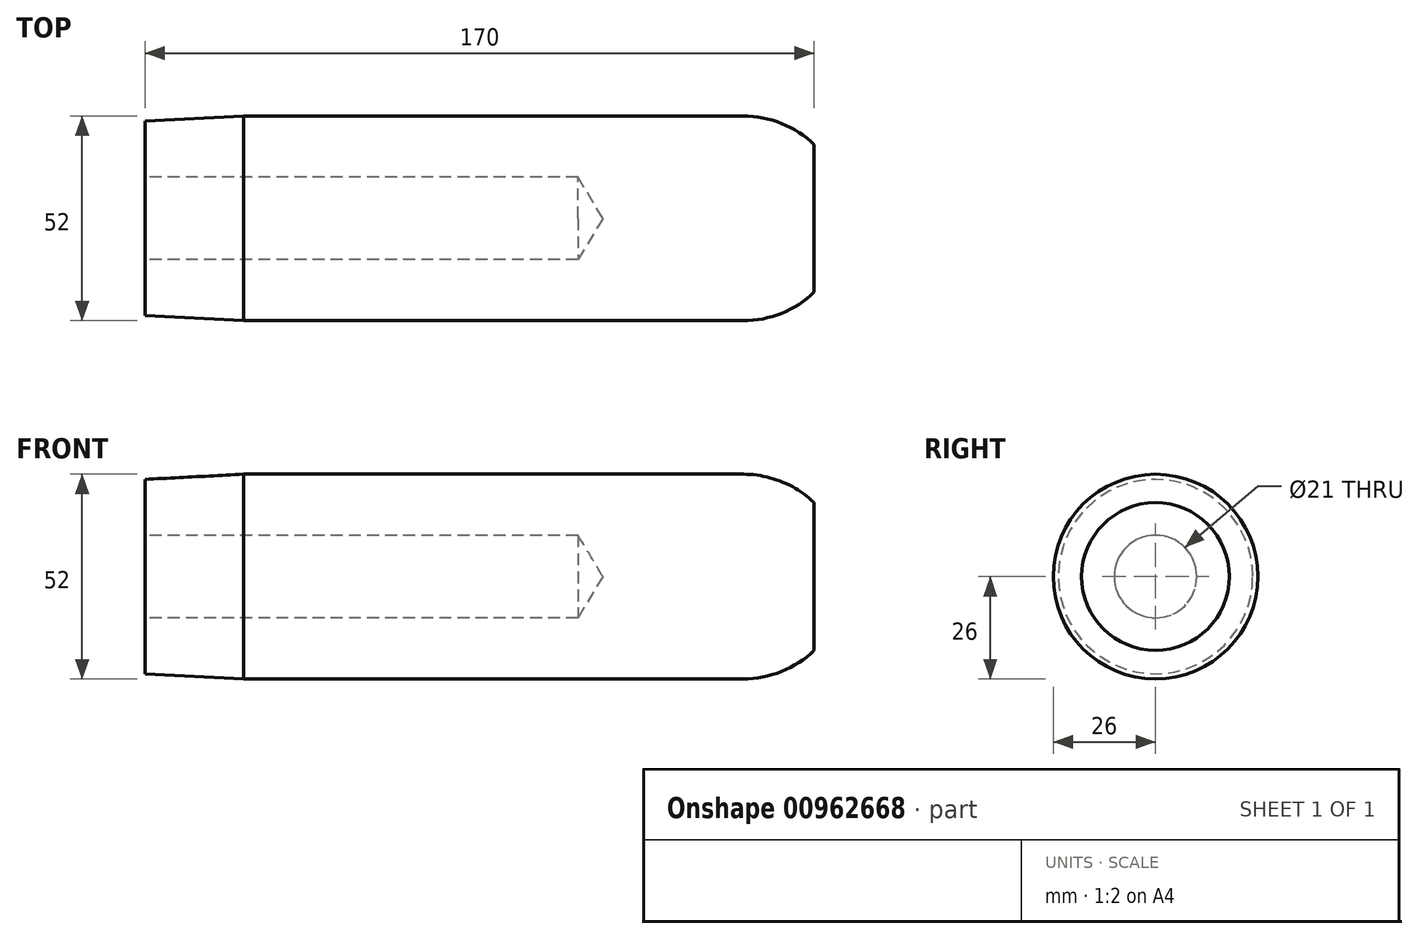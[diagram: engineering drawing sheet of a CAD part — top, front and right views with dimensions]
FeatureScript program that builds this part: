
annotation { "Feature Type Name" : "Feature", "Feature Type Description" : "" }
export const myFeature = defineFeature(function(context is Context, id is Id, definition is map)
    precondition{}
    {
        {
            var Q0;
            Q0=qCreatedBy(makeId("Front.planeOp"),FACE);
            var sketch = newSketch(context, id + "F0", { "sketchPlane" : qUnion([Q0])});
            skLineSegment(sketch, "E0", {"start": v(0, 0) * mm, "end": v(170, 0) * mm});
            skLineSegment(sketch, "E1", {"start": v(0, 0) * mm, "end": v(0, -24.69) * mm});
            skLineSegment(sketch, "E2", {"start": v(0, -24.69) * mm, "end": v(25, -26) * mm});
            skLineSegment(sketch, "E3", {"start": v(25, -26) * mm, "end": v(152, -26) * mm});
            skArc(sketch, "E4", {"start": v(152, -26) * mm, "mid": v(161.7, -24.12) * mm, "end": v(170, -18.76) * mm});
            skLineSegment(sketch, "E5", {"start": v(170, 0) * mm, "end": v(170, -18.76) * mm});
            skSolve(sketch);
        }
        {
            var Q0;
            Q0=makeQuery(id+"F0.imprint","IMPRINT",FACE,{"disambiguationData":[TD([[makeQuery(id+"F0.imprint","IMPRINT",EDGE,{"derivedFrom":sQuery(id+"F0.wireOp",EDGE,"E0")}),-1.0]])]});
            var Q1;
            Q1=sQuery(id+"F0.wireOp",EDGE,"E0");
            revolve(context, id + "F1", {"surfaceOperationType" : NewSurfaceOperationType.NEW, "entities" : qUnion([Q0]), "axis" : qUnion([Q1]), "revolveType" : RevolveType.FULL});
        }
        {
            var Q0;
            Q0=makeQuery(id+"F1.opRevolve","SWEPT_FACE",FACE,{"disambiguationData":[OSD([sQuery(id+"F0.wireOp",EDGE,"E1")])]});
            var sketch = newSketch(context, id + "F2", { "sketchPlane" : qUnion([Q0])});
            skCircle(sketch, "E6", {"center": v(0, 0) * mm, "radius": 10.5 * mm});
            skSolve(sketch);
        }
        {
            var Q0;
            Q0=makeQuery(id+"F2.imprint","IMPRINT",FACE,{"disambiguationData":[TD([[makeQuery(id+"F2.imprint","IMPRINT",EDGE,{"derivedFrom":sQuery(id+"F2.wireOp",EDGE,"E6")}),1.0]])]});
            extrude(context, id + "F3", {"entities" : qUnion([Q0]), "operationType" : NewBodyOperationType.REMOVE, "oppositeDirection" : true, "depth" : 110 * mm, "offsetDistance" : 25 * mm});
        }
        {
            var Q0;
            Q0=qCreatedBy(makeId("Front.planeOp"),FACE);
            var sketch = newSketch(context, id + "F4", { "sketchPlane" : qUnion([Q0])});
            skLineSegment(sketch, "E7", {"start": v(116.3, 0) * mm, "end": v(110, 10.5) * mm});
            skLineSegment(sketch, "E8", {"start": v(110, 10.5) * mm, "end": v(110, 0) * mm});
            skLineSegment(sketch, "E9", {"start": v(110, 0) * mm, "end": v(116.3, 0) * mm});
            skSolve(sketch);
        }
        {
            var Q0;
            Q0 = qSketchRegion(id + "F4", true);
            var Q1;
            Q1=sQuery(id+"F4.wireOp",EDGE,"E9");
            revolve(context, id + "F5", {"operationType" : NewBodyOperationType.REMOVE, "surfaceOperationType" : NewSurfaceOperationType.NEW, "entities" : qUnion([Q0]), "axis" : qUnion([Q1]), "revolveType" : RevolveType.FULL, "oppositeDirection" : true});
        }
    });
